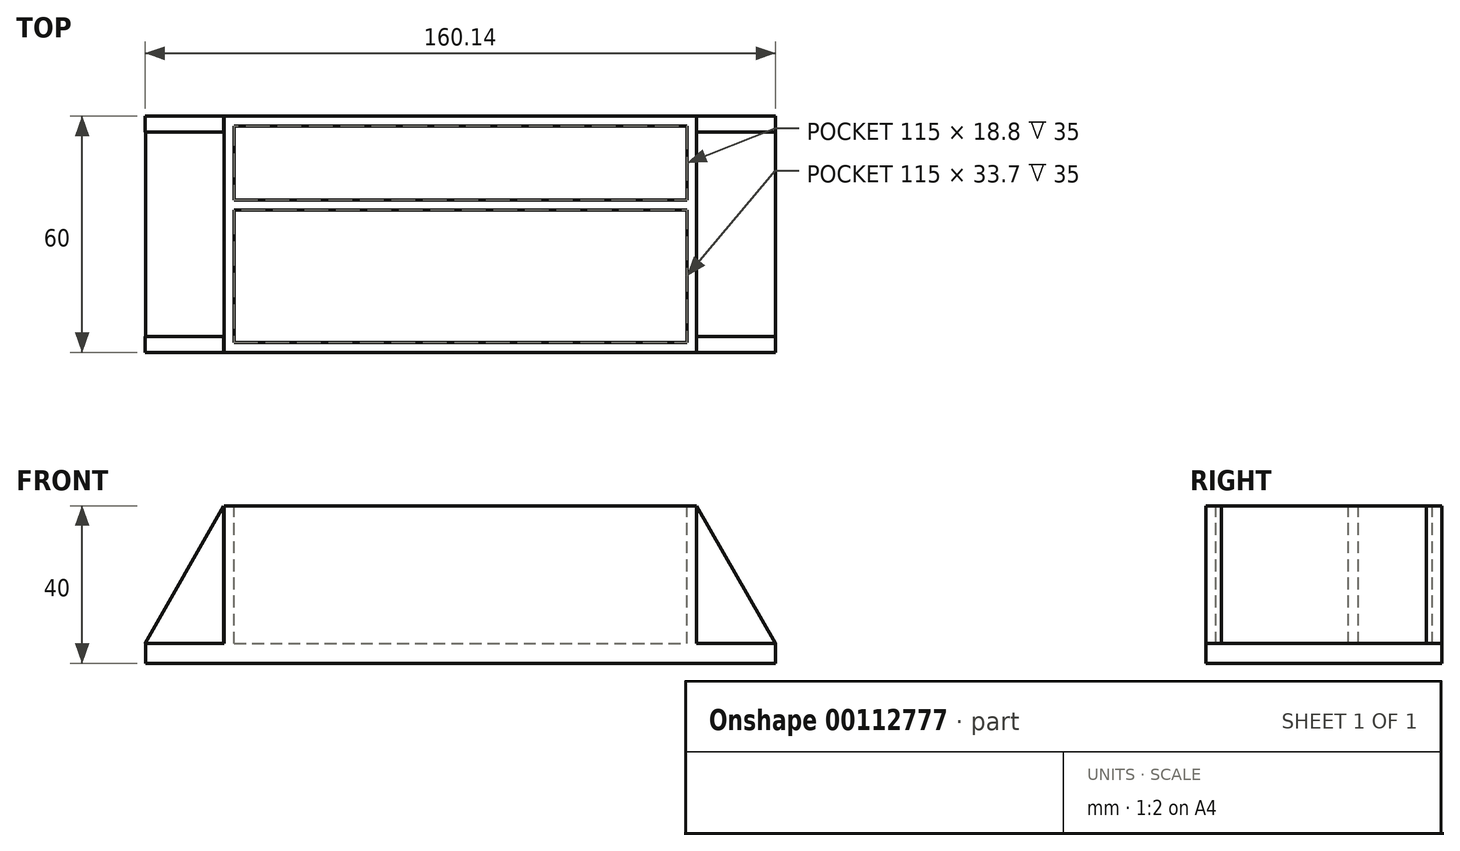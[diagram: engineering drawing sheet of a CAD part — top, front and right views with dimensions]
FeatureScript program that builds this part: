
annotation { "Feature Type Name" : "Feature", "Feature Type Description" : "" }
export const myFeature = defineFeature(function(context is Context, id is Id, definition is map)
    precondition{}
    {
        {
            var Q0;
            Q0=qCreatedBy(makeId("Front.planeOp"),FACE);
            var sketch = newSketch(context, id + "F0", { "sketchPlane" : qUnion([Q0])});
            skLineSegment(sketch, "E0", {"start": v(-93.93, -61.95) * mm, "end": v(66.07, -61.95) * mm});
            skLineSegment(sketch, "E1", {"start": v(66.07, -61.95) * mm, "end": v(66.07, -56.95) * mm});
            skLineSegment(sketch, "E2", {"start": v(66.07, -56.95) * mm, "end": v(46.07, -56.95) * mm});
            skLineSegment(sketch, "E3", {"start": v(46.07, -56.95) * mm, "end": v(46.07, -21.95) * mm});
            skLineSegment(sketch, "E4", {"start": v(46.07, -21.95) * mm, "end": v(-73.93, -21.95) * mm});
            skLineSegment(sketch, "E5", {"start": v(-73.93, -21.95) * mm, "end": v(-73.93, -56.95) * mm});
            skPoint(sketch, "E5.endSnap0", {"position": v(56.07, -56.95) * mm});
            skLineSegment(sketch, "E6", {"start": v(-73.93, -56.95) * mm, "end": v(-93.93, -56.95) * mm});
            skLineSegment(sketch, "E7", {"start": v(-93.93, -56.95) * mm, "end": v(-93.93, -61.95) * mm});
            skSolve(sketch);
        }
        {
            var Q0;
            Q0=makeQuery(id+"F0.imprint","IMPRINT",FACE,{"disambiguationData":[TD([[makeQuery(id+"F0.imprint","IMPRINT",EDGE,{"derivedFrom":sQuery(id+"F0.wireOp",EDGE,"E0")}),1.0]])]});
            extrude(context, id + "F1", {"entities" : qUnion([Q0]), "oppositeDirection" : true, "depth" : 60 * mm});
        }
        {
            var Q0;
            Q0=makeQuery(id+"F1.opExtrude","CAP_FACE",FACE,{"disambiguationData":[OSD([sQuery(id+"F0.wireOp",EDGE,"E0"),sQuery(id+"F0.wireOp",EDGE,"E1"),sQuery(id+"F0.wireOp",EDGE,"E2"),sQuery(id+"F0.wireOp",EDGE,"E3"),sQuery(id+"F0.wireOp",EDGE,"E4"),sQuery(id+"F0.wireOp",EDGE,"E5"),sQuery(id+"F0.wireOp",EDGE,"E6"),sQuery(id+"F0.wireOp",EDGE,"E7")])],"isStart":true});
            var sketch = newSketch(context, id + "F2", { "sketchPlane" : qUnion([Q0])});
            skLineSegment(sketch, "E8", {"start": v(46.07, -21.95) * mm, "end": v(66.07, -56.95) * mm});
            skLineSegment(sketch, "E9", {"start": v(66.07, -56.95) * mm, "end": v(46.07, -56.95) * mm});
            skLineSegment(sketch, "E10", {"start": v(46.07, -56.95) * mm, "end": v(46.07, -21.95) * mm});
            skSolve(sketch);
        }
        {
            var Q0;
            Q0=makeQuery(id+"F2.imprint","IMPRINT",FACE,{"disambiguationData":[TD([[makeQuery(id+"F2.imprint","IMPRINT",EDGE,{"derivedFrom":sQuery(id+"F2.wireOp",EDGE,"E8")}),-1.0]])]});
            extrude(context, id + "F3", {"entities" : qUnion([Q0]), "oppositeDirection" : true, "depth" : 4 * mm});
        }
        {
            var Q0;
            Q0=makeQuery(id+"F3.opExtrude","SWEPT_BODY",BODY,{"disambiguationData":[OSD([sQuery(id+"F2.wireOp",EDGE,"E8"),sQuery(id+"F2.wireOp",EDGE,"E9"),sQuery(id+"F2.wireOp",EDGE,"E10")])]});
            var Q1;
            Q1=qCreatedBy(makeId("Front.planeOp"),FACE);
            transform(context, id + "F4", {"entities" : qUnion([Q0]), "transformType" : TransformType.TRANSLATION_DISTANCE, "transformDirection" : qUnion([Q1]), "distance" : 56 * mm, "oppositeDirection" : true, "makeCopy" : true});
        }
        {
            var Q0;
            Q0=makeQuery(id+"F3.opExtrude","SWEPT_BODY",BODY,{"disambiguationData":[OSD([sQuery(id+"F2.wireOp",EDGE,"E8"),sQuery(id+"F2.wireOp",EDGE,"E9"),sQuery(id+"F2.wireOp",EDGE,"E10")])]});
            var Q1;
            Q1=makeQuery(id+"F4.opPattern","COPY",BODY,{"derivedFrom":makeQuery(id+"F3.opExtrude","SWEPT_BODY",BODY,{"disambiguationData":[OSD([sQuery(id+"F2.wireOp",EDGE,"E8"),sQuery(id+"F2.wireOp",EDGE,"E9"),sQuery(id+"F2.wireOp",EDGE,"E10")])]}),"instanceName":"1"});
            var Q2;
            Q2=qCreatedBy(makeId("Right.planeOp"),FACE);
            mirror(context, id + "F5", {"entities" : qUnion([Q0, Q1]), "mirrorPlane" : qUnion([Q2])});
        }
        {
            var Q0;
            Q0=makeQuery(id+"F5.opPattern","COPY",BODY,{"derivedFrom":makeQuery(id+"F3.opExtrude","SWEPT_BODY",BODY,{"disambiguationData":[OSD([sQuery(id+"F2.wireOp",EDGE,"E8"),sQuery(id+"F2.wireOp",EDGE,"E9"),sQuery(id+"F2.wireOp",EDGE,"E10")])]}),"instanceName":"1"});
            var Q1;
            Q1=makeQuery(id+"F5.opPattern","COPY",BODY,{"derivedFrom":makeQuery(id+"F4.opPattern","COPY",BODY,{"derivedFrom":makeQuery(id+"F3.opExtrude","SWEPT_BODY",BODY,{"disambiguationData":[OSD([sQuery(id+"F2.wireOp",EDGE,"E8"),sQuery(id+"F2.wireOp",EDGE,"E9"),sQuery(id+"F2.wireOp",EDGE,"E10")])]}),"instanceName":"1"}),"instanceName":"1"});
            var Q2;
            Q2=qCreatedBy(makeId("Right.planeOp"),FACE);
            transform(context, id + "F6", {"entities" : qUnion([Q0, Q1]), "transformType" : TransformType.TRANSLATION_DISTANCE, "transformDirection" : qUnion([Q2]), "distance" : 28 * mm, "oppositeDirection" : true, "makeCopy" : false});
        }
        {
            var Q0;
            Q0=makeQuery(id+"F1.opExtrude","SWEPT_FACE",FACE,{"disambiguationData":[OSD([sQuery(id+"F0.wireOp",EDGE,"E4")])]});
            var sketch = newSketch(context, id + "F7", { "sketchPlane" : qUnion([Q0])});
            skLineSegment(sketch, "E11.bottom", {"start": v(-71.43, 57.5) * mm, "end": v(43.57, 57.5) * mm});
            skLineSegment(sketch, "E11.top", {"start": v(-71.43, 38.7) * mm, "end": v(43.57, 38.7) * mm});
            skLineSegment(sketch, "E11.left", {"start": v(-71.43, 57.5) * mm, "end": v(-71.43, 38.7) * mm});
            skLineSegment(sketch, "E11.right", {"start": v(43.57, 57.5) * mm, "end": v(43.57, 38.7) * mm});
            skPoint(sketch, "E12.firstSnap0", {"position": v(-71.43, 48.1) * mm});
            skLineSegment(sketch, "E12.bottom", {"start": v(-71.43, 36.2) * mm, "end": v(43.57, 36.2) * mm});
            skLineSegment(sketch, "E12.top", {"start": v(-71.43, 2.5) * mm, "end": v(43.57, 2.5) * mm});
            skLineSegment(sketch, "E12.left", {"start": v(-71.43, 36.2) * mm, "end": v(-71.43, 2.5) * mm});
            skLineSegment(sketch, "E12.right", {"start": v(43.57, 36.2) * mm, "end": v(43.57, 2.5) * mm});
            skSolve(sketch);
        }
        {
            var Q0;
            Q0=makeQuery(id+"F7.imprint","IMPRINT",FACE,{"disambiguationData":[TD([[makeQuery(id+"F7.imprint","IMPRINT",EDGE,{"derivedFrom":sQuery(id+"F7.wireOp",EDGE,"E12.bottom")}),-1.0]])]});
            var Q1;
            Q1=makeQuery(id+"F7.imprint","IMPRINT",FACE,{"disambiguationData":[TD([[makeQuery(id+"F7.imprint","IMPRINT",EDGE,{"derivedFrom":sQuery(id+"F7.wireOp",EDGE,"E11.bottom")}),-1.0]])]});
            extrude(context, id + "F8", {"entities" : qUnion([Q0, Q1]), "operationType" : NewBodyOperationType.REMOVE, "oppositeDirection" : true, "depth" : 35 * mm});
        }
    });
